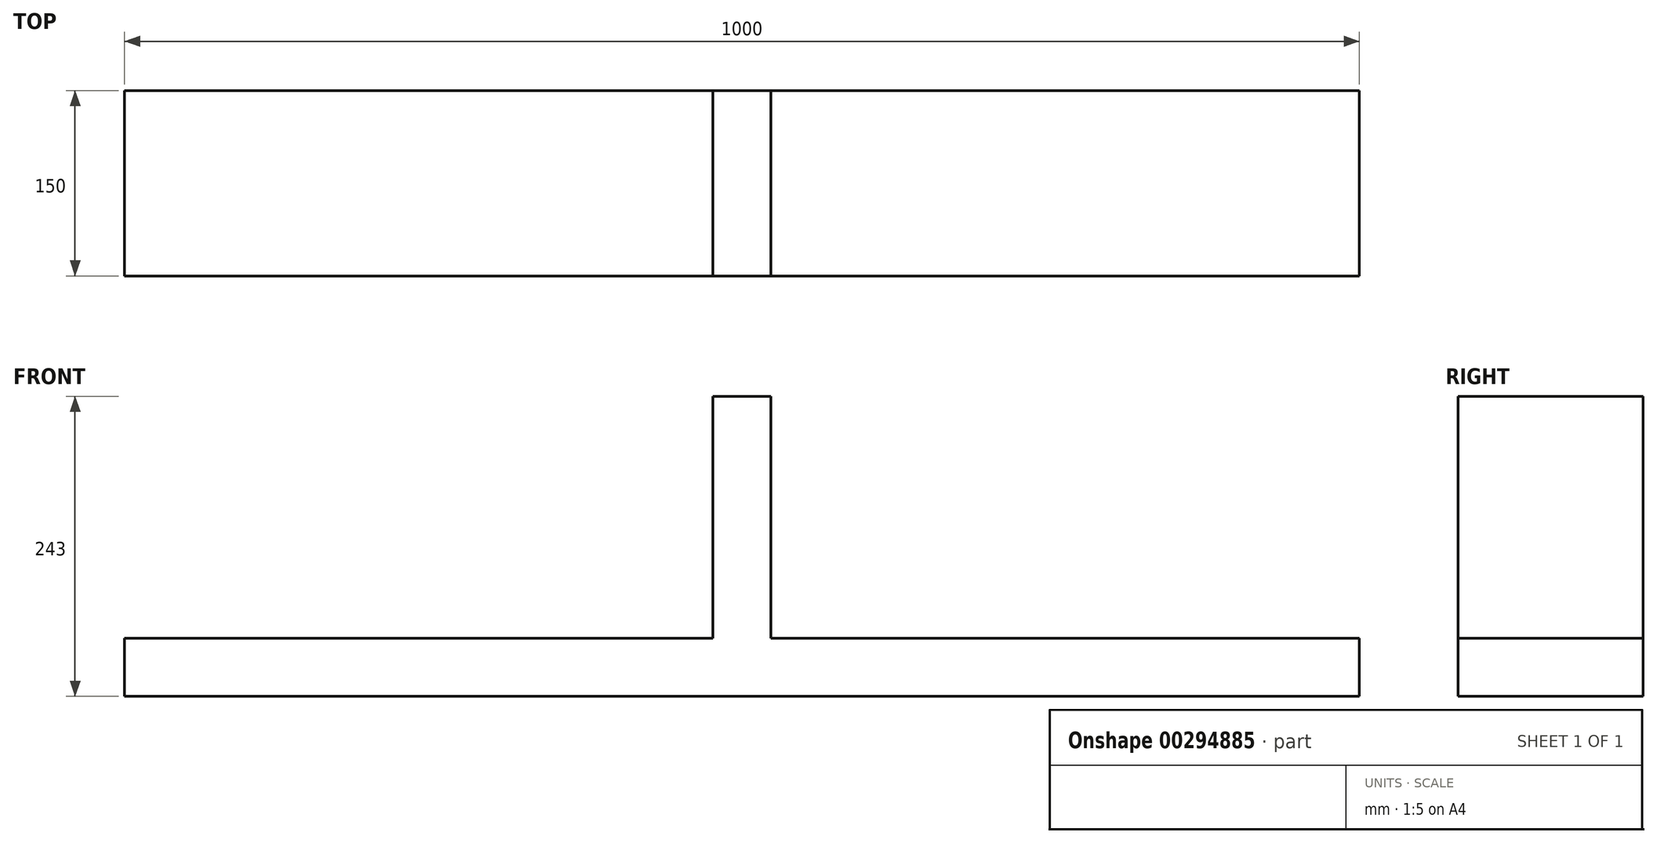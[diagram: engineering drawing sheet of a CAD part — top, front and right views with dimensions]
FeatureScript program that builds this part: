
annotation { "Feature Type Name" : "Feature", "Feature Type Description" : "" }
export const myFeature = defineFeature(function(context is Context, id is Id, definition is map)
    precondition{}
    {
        {
            var Q0;
            Q0=qCreatedBy(makeId("Front.planeOp"),FACE);
            var sketch = newSketch(context, id + "F0", { "sketchPlane" : qUnion([Q0])});
            skLineSegment(sketch, "E0", {"start": v(0, 0) * mm, "end": v(500, 0) * mm});
            skLineSegment(sketch, "E1", {"start": v(500, 0) * mm, "end": v(500, 47) * mm});
            skLineSegment(sketch, "E2", {"start": v(500, 47) * mm, "end": v(23.5, 47) * mm});
            skLineSegment(sketch, "E3", {"start": v(23.5, 47) * mm, "end": v(23.5, 243) * mm});
            skLineSegment(sketch, "E4", {"start": v(23.5, 243) * mm, "end": v(0, 243) * mm});
            skLineSegment(sketch, "E5", {"start": v(0, 243) * mm, "end": v(0, 0) * mm, "construction": true});
            skLineSegment(sketch, "E6.MirrorCS", {"start": v(-23.5, 243) * mm, "end": v(0, 243) * mm});
            skLineSegment(sketch, "E7.MirrorCS", {"start": v(-23.5, 47) * mm, "end": v(-23.5, 243) * mm});
            skLineSegment(sketch, "E8.MirrorCS", {"start": v(-500, 0) * mm, "end": v(-500, 47) * mm});
            skLineSegment(sketch, "E9.MirrorCS", {"start": v(0, 0) * mm, "end": v(-500, 0) * mm});
            skLineSegment(sketch, "E10.MirrorCS", {"start": v(-500, 47) * mm, "end": v(-23.5, 47) * mm});
            skSolve(sketch);
        }
        {
            var Q0;
            Q0 = qSketchRegion(id + "F0", true);
            extrude(context, id + "F1", {"entities" : qUnion([Q0]), "depth" : 150 * mm});
        }
    });
